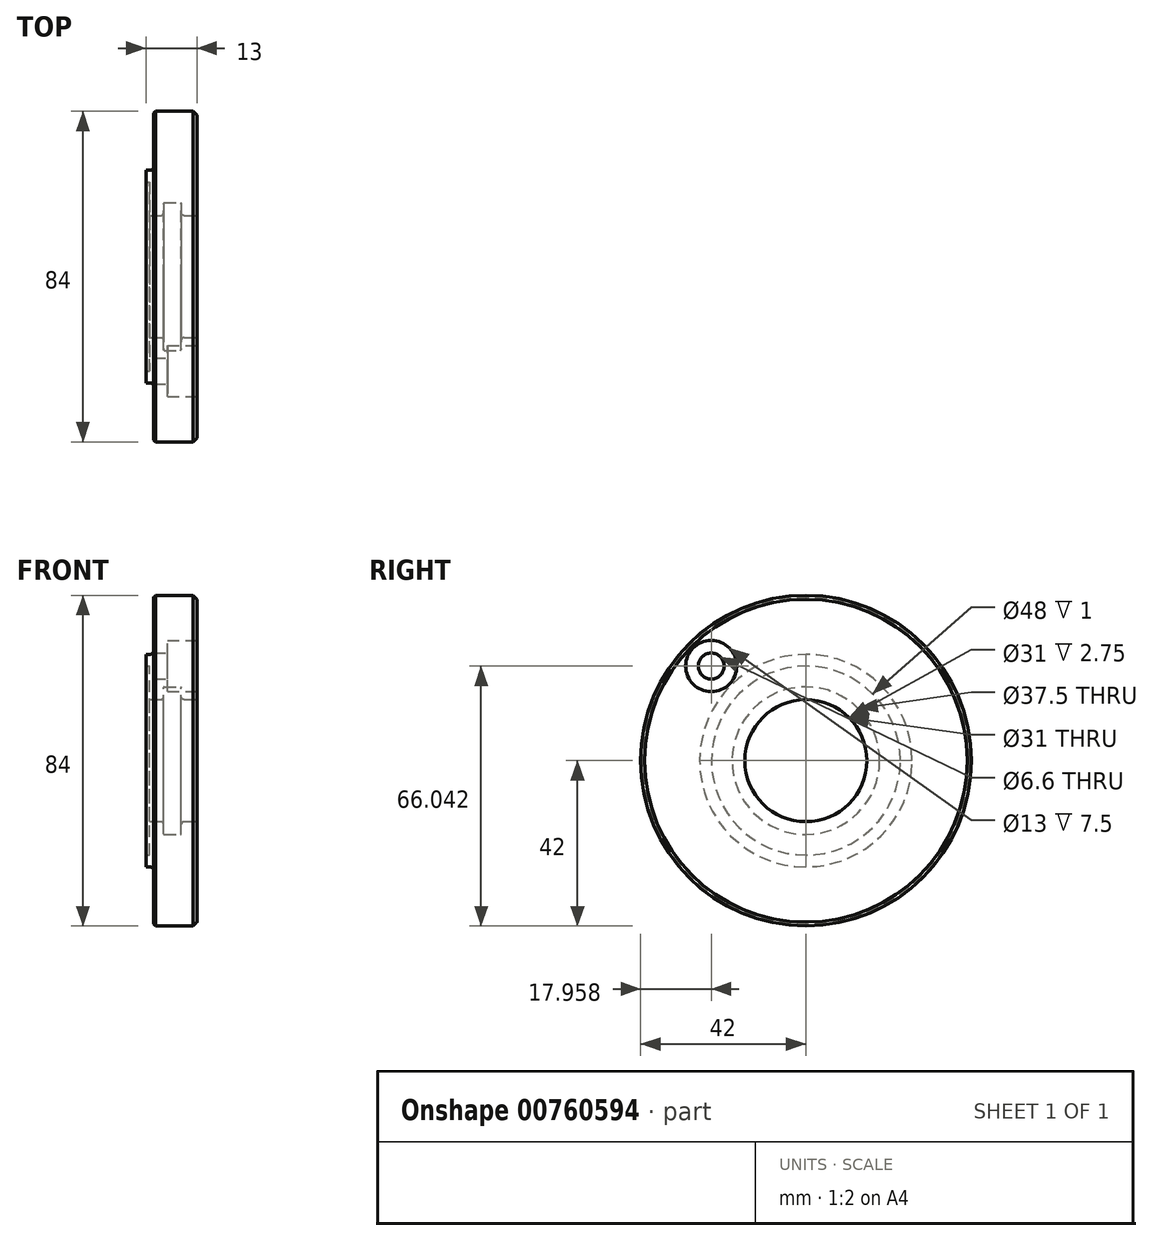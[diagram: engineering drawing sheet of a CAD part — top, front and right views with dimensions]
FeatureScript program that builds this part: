
annotation { "Feature Type Name" : "Feature", "Feature Type Description" : "" }
export const myFeature = defineFeature(function(context is Context, id is Id, definition is map)
    precondition{}
    {
        {
            var Q0;
            Q0=qCreatedBy(makeId("Front.planeOp"),FACE);
            var sketch = newSketch(context, id + "F0", { "sketchPlane" : qUnion([Q0])});
            skLineSegment(sketch, "E0", {"start": v(0, 15.5) * mm, "end": v(0, 42) * mm});
            skLineSegment(sketch, "E1", {"start": v(0, 42) * mm, "end": v(-11, 42) * mm});
            skLineSegment(sketch, "E2", {"start": v(-11, 42) * mm, "end": v(-11, 28) * mm});
            skLineSegment(sketch, "E3", {"start": v(-12, 27) * mm, "end": v(-13, 27) * mm});
            skLineSegment(sketch, "E4", {"start": v(-13, 27) * mm, "end": v(-13, 24) * mm});
            skLineSegment(sketch, "E5", {"start": v(-13, 24) * mm, "end": v(-12, 24) * mm});
            skLineSegment(sketch, "E6", {"start": v(-12, 24) * mm, "end": v(-12, 15.5) * mm});
            skLineSegment(sketch, "E7", {"start": v(-12, 15.5) * mm, "end": v(-9.25, 15.5) * mm});
            skLineSegment(sketch, "E8", {"start": v(-8.5, 16.25) * mm, "end": v(-8.5, 18.55) * mm});
            skLineSegment(sketch, "E9", {"start": v(-8.3, 18.75) * mm, "end": v(-4.2, 18.75) * mm});
            skLineSegment(sketch, "E10", {"start": v(-4, 18.55) * mm, "end": v(-4, 16.25) * mm});
            skLineSegment(sketch, "E11", {"start": v(-3.25, 15.5) * mm, "end": v(0, 15.5) * mm});
            skLineSegment(sketch, "E12", {"start": v(0, 0) * mm, "end": v(-13, 0) * mm, "construction": true});
            skPoint(sketch, "E12.endSnap0", {"position": v(-13, 25.5) * mm});
            skPoint(sketch, "E13.visualSharp", {"position": v(-11, 27) * mm});
            skArc(sketch, "E13.filletArc", {"start": v(-12, 27) * mm, "mid": v(-11.3, 27.3) * mm, "end": v(-11, 28) * mm});
            skPoint(sketch, "E14.visualSharp", {"position": v(-8.5, 18.75) * mm});
            skArc(sketch, "E14.filletArc", {"start": v(-8.3, 18.75) * mm, "mid": v(-8.44, 18.7) * mm, "end": v(-8.5, 18.55) * mm});
            skPoint(sketch, "E15.visualSharp", {"position": v(-4, 18.75) * mm});
            skArc(sketch, "E15.filletArc", {"start": v(-4, 18.55) * mm, "mid": v(-4.06, 18.7) * mm, "end": v(-4.2, 18.75) * mm});
            skPoint(sketch, "E16.visualSharp", {"position": v(-8.5, 15.5) * mm});
            skArc(sketch, "E16.filletArc", {"start": v(-9.25, 15.5) * mm, "mid": v(-8.72, 15.72) * mm, "end": v(-8.5, 16.25) * mm});
            skPoint(sketch, "E17.visualSharp", {"position": v(-4, 15.5) * mm});
            skArc(sketch, "E17.filletArc", {"start": v(-4, 16.25) * mm, "mid": v(-3.78, 15.72) * mm, "end": v(-3.25, 15.5) * mm});
            skSolve(sketch);
        }
        {
            var Q0;
            Q0=makeQuery(id+"F0.imprint","IMPRINT",FACE,{"disambiguationData":[TD([[makeQuery(id+"F0.imprint","IMPRINT",EDGE,{"derivedFrom":sQuery(id+"F0.wireOp",EDGE,"E0")}),1.0]])]});
            var Q1;
            Q1=sQuery(id+"F0.wireOp",EDGE,"E12");
            revolve(context, id + "F1", {"surfaceOperationType" : NewSurfaceOperationType.NEW, "entities" : qUnion([Q0]), "axis" : qUnion([Q1]), "revolveType" : RevolveType.FULL});
        }
        {
            var Q0;
            Q0=makeQuery(id+"F1.opRevolve","SWEPT_EDGE",EDGE,{"disambiguationData":[OSD([sQuery(id+"F0.wireOp",EDGE,"E0"),sQuery(id+"F0.wireOp",EDGE,"E1")])]});
            chamfer(context, id + "F2", {"entities" : qUnion([Q0]), "width" : 1 * mm, "tangentPropagation" : true});
        }
        {
            var Q0;
            Q0=makeQuery(id+"F1.opRevolve","SWEPT_EDGE",EDGE,{"disambiguationData":[OSD([sQuery(id+"F0.wireOp",EDGE,"E1"),sQuery(id+"F0.wireOp",EDGE,"E2")])]});
            chamfer(context, id + "F3", {"entities" : qUnion([Q0]), "width" : 0.5 * mm, "tangentPropagation" : true});
        }
        {
            var Q0;
            Q0=qCreatedBy(makeId("Right.planeOp"),FACE);
            var sketch = newSketch(context, id + "F4", { "sketchPlane" : qUnion([Q0])});
            skPoint(sketch, "E18", {"position": v(-24.04, 24.04) * mm});
            skLineSegment(sketch, "E19", {"start": v(0, 0) * mm, "end": v(-24.04, 24.04) * mm, "construction": true});
            skSolve(sketch);
        }
        {
            var Q0;
            Q0=sQuery(id+"F4.wireOp",VERTEX,"E18");
            var Q1;
            Q1=makeQuery(id+"F1.opRevolve","SWEPT_BODY",BODY,{"disambiguationData":[OSD([sQuery(id+"F0.wireOp",EDGE,"E0"),sQuery(id+"F0.wireOp",EDGE,"E1"),sQuery(id+"F0.wireOp",EDGE,"E2"),sQuery(id+"F0.wireOp",EDGE,"E3"),sQuery(id+"F0.wireOp",EDGE,"E4"),sQuery(id+"F0.wireOp",EDGE,"E5"),sQuery(id+"F0.wireOp",EDGE,"E6"),sQuery(id+"F0.wireOp",EDGE,"E7"),sQuery(id+"F0.wireOp",EDGE,"E8"),sQuery(id+"F0.wireOp",EDGE,"E9"),sQuery(id+"F0.wireOp",EDGE,"E10"),sQuery(id+"F0.wireOp",EDGE,"E11"),sQuery(id+"F0.wireOp",EDGE,"E13.filletArc"),sQuery(id+"F0.wireOp",EDGE,"E14.filletArc"),sQuery(id+"F0.wireOp",EDGE,"E15.filletArc"),sQuery(id+"F0.wireOp",EDGE,"E16.filletArc"),sQuery(id+"F0.wireOp",EDGE,"E17.filletArc")])]});
            hole(context, id + "F5", {"style" : HoleStyle.C_BORE, "endStyle" : HoleEndStyle.THROUGH, "holeDiameter" : 6.6 * mm, "cBoreDiameter" : 13 * mm, "cBoreDepth" : 7.5 * mm, "majorDiameter" : 5 * mm, "isTappedThrough" : true, "tappedDepth" : 12 * mm, "tapClearance" : 6, "startFromSketch" : true, "locations" : qUnion([Q0]), "scope" : qUnion([Q1])});
        }
    });
